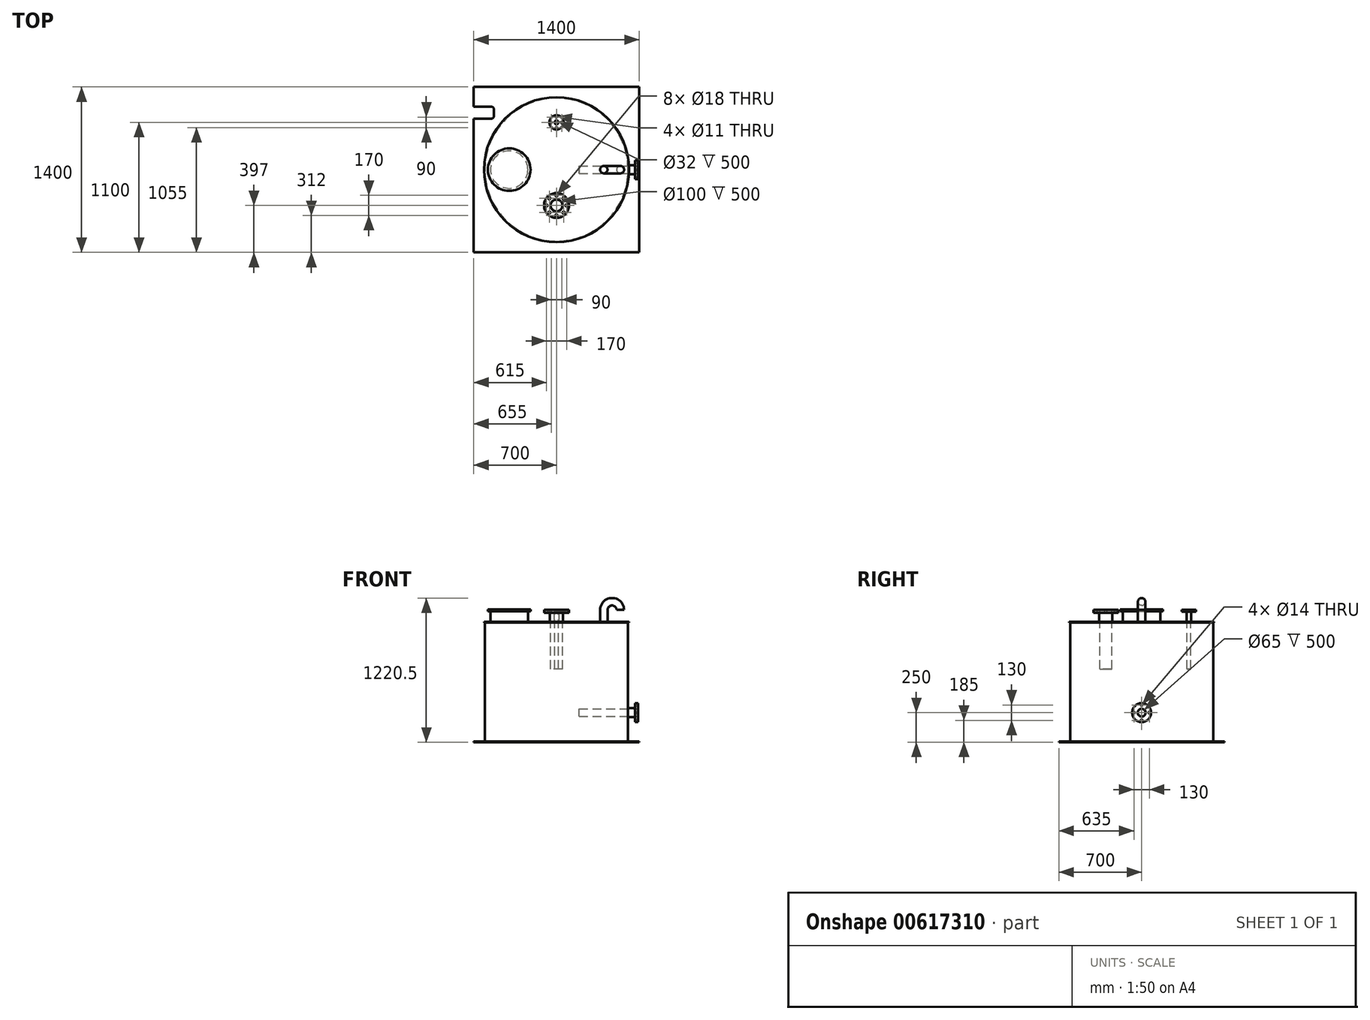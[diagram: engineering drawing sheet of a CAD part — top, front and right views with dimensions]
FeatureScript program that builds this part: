
annotation { "Feature Type Name" : "Feature", "Feature Type Description" : "" }
export const myFeature = defineFeature(function(context is Context, id is Id, definition is map)
    precondition{}
    {
        {
            var Q0;
            Q0=qCreatedBy(makeId("Front.planeOp"),FACE);
            var sketch = newSketch(context, id + "F0", { "sketchPlane" : qUnion([Q0])});
            skLineSegment(sketch, "E0.bottom", {"start": v(0, 0) * mm, "end": v(605, 0) * mm});
            skLineSegment(sketch, "E0.top", {"start": v(0, 1014) * mm, "end": v(605, 1014) * mm});
            skLineSegment(sketch, "E0.left", {"start": v(0, 0) * mm, "end": v(0, 1014) * mm});
            skLineSegment(sketch, "E0.right", {"start": v(605, 0) * mm, "end": v(605, 1006) * mm});
            skLineSegment(sketch, "E1.bottom", {"start": v(605, 1014) * mm, "end": v(613, 1014) * mm});
            skLineSegment(sketch, "E1.top", {"start": v(605, 1006) * mm, "end": v(613, 1006) * mm});
            skLineSegment(sketch, "E1.right", {"start": v(613, 1014) * mm, "end": v(613, 1006) * mm});
            skSolve(sketch);
        }
        {
            var Q0;
            Q0=makeQuery(id+"F0.imprint","IMPRINT",FACE,{"disambiguationData":[TD([[makeQuery(id+"F0.imprint","IMPRINT",EDGE,{"derivedFrom":sQuery(id+"F0.wireOp",EDGE,"E0.bottom")}),1.0]])]});
            var Q1;
            Q1=sQuery(id+"F0.wireOp",EDGE,"E0.left");
            revolve(context, id + "F1", {"entities" : qUnion([Q0]), "axis" : qUnion([Q1]), "revolveType" : RevolveType.FULL});
        }
        {
            var Q0;
            Q0=makeQuery(id+"F1.opRevolve","SWEPT_FACE",FACE,{"disambiguationData":[OSD([sQuery(id+"F0.wireOp",EDGE,"E0.bottom")])]});
            var sketch = newSketch(context, id + "F2", { "sketchPlane" : qUnion([Q0])});
            skLineSegment(sketch, "E2.bottom", {"start": v(700, 700) * mm, "end": v(-700, 700) * mm});
            skLineSegment(sketch, "E2.top", {"start": v(700, -700) * mm, "end": v(-700, -700) * mm});
            skLineSegment(sketch, "E2.left", {"start": v(700, 700) * mm, "end": v(700, -700) * mm});
            skLineSegment(sketch, "E2.right", {"start": v(-700, 700) * mm, "end": v(-700, -700) * mm});
            skPoint(sketch, "E2.middle", {"position": v(0, 0) * mm});
            skSolve(sketch);
        }
        {
            var Q0;
            Q0=makeQuery(id+"F2.imprint","IMPRINT",FACE,{"disambiguationData":[TD([[makeQuery(id+"F2.imprint","IMPRINT",EDGE,{"derivedFrom":sQuery(id+"F2.wireOp",EDGE,"E2.bottom")}),1.0]])]});
            var Q1;
            Q1=makeQuery(id+"F2.imprint","IMPRINT",FACE,{"disambiguationData":[TD([[makeQuery(id+"F2.imprint","IMPRINT",EDGE,{"derivedFrom":makeQuery(id+"F1.opRevolve","SWEPT_EDGE",EDGE,{"disambiguationData":[OSD([sQuery(id+"F0.wireOp",EDGE,"E0.bottom"),sQuery(id+"F0.wireOp",EDGE,"E0.right")])]})}),1.0]])]});
            extrude(context, id + "F3", {"entities" : qUnion([Q0, Q1]), "operationType" : NewBodyOperationType.ADD, "depth" : 5 * mm, "offsetDistance" : 25 * mm});
        }
        {
            var Q0;
            Q0=makeQuery(id+"F3.opExtrude","CAP_FACE",FACE,{"disambiguationData":[OSD([sQuery(id+"F2.wireOp",EDGE,"E2.bottom"),sQuery(id+"F2.wireOp",EDGE,"E2.top"),sQuery(id+"F2.wireOp",EDGE,"E2.left"),sQuery(id+"F2.wireOp",EDGE,"E2.right")])],"isStart":true});
            var sketch = newSketch(context, id + "F4", { "sketchPlane" : qUnion([Q0])});
            skLineSegment(sketch, "E3.bottom", {"start": v(-700, 532) * mm, "end": v(-550, 532) * mm});
            skLineSegment(sketch, "E3.top", {"start": v(-700, 432) * mm, "end": v(-550, 432) * mm});
            skLineSegment(sketch, "E3.right", {"start": v(-530, 512) * mm, "end": v(-530, 452) * mm});
            skPoint(sketch, "E4.visualSharp", {"position": v(-530, 432) * mm});
            skArc(sketch, "E4.filletArc", {"start": v(-550, 432) * mm, "mid": v(-535.86, 437.86) * mm, "end": v(-530, 452) * mm});
            skPoint(sketch, "E5.visualSharp", {"position": v(-530, 532) * mm});
            skArc(sketch, "E5.filletArc", {"start": v(-530, 512) * mm, "mid": v(-535.86, 526.14) * mm, "end": v(-550, 532) * mm});
            skLineSegment(sketch, "E6", {"start": v(-700, 432) * mm, "end": v(-700, 532) * mm});
            skSolve(sketch);
        }
        {
            var Q0;
            Q0=makeQuery(id+"F4.imprint","IMPRINT",FACE,{"disambiguationData":[TD([[makeQuery(id+"F4.imprint","IMPRINT",EDGE,{"derivedFrom":sQuery(id+"F4.wireOp",EDGE,"E3.bottom")}),-1.0]])]});
            extrude(context, id + "F5", {"entities" : qUnion([Q0]), "operationType" : NewBodyOperationType.REMOVE, "oppositeDirection" : true, "depth" : 25 * mm, "offsetDistance" : 25 * mm});
        }
        {
            var Q0;
            Q0=makeQuery(id+"F1.opRevolve","SWEPT_FACE",FACE,{"disambiguationData":[OSD([sQuery(id+"F0.wireOp",EDGE,"E0.top"),sQuery(id+"F0.wireOp",EDGE,"E1.bottom")])]});
            var sketch = newSketch(context, id + "F6", { "sketchPlane" : qUnion([Q0])});
            skCircle(sketch, "E7", {"center": v(-400, 0) * mm, "radius": 158 * mm});
            skSolve(sketch);
        }
        {
            var Q0;
            Q0=makeQuery(id+"F6.imprint","IMPRINT",FACE,{"disambiguationData":[TD([[makeQuery(id+"F6.imprint","IMPRINT",EDGE,{"derivedFrom":sQuery(id+"F6.wireOp",EDGE,"E7")}),1.0]])]});
            extrude(context, id + "F7", {"entities" : qUnion([Q0]), "operationType" : NewBodyOperationType.ADD, "depth" : 90 * mm, "offsetDistance" : 25 * mm});
        }
        {
            var Q0;
            Q0=makeQuery(id+"F7.opExtrude","CAP_FACE",FACE,{"disambiguationData":[OSD([sQuery(id+"F6.wireOp",EDGE,"E7")])],"isStart":false});
            var sketch = newSketch(context, id + "F8", { "sketchPlane" : qUnion([Q0])});
            skCircle(sketch, "E8", {"center": v(-400, 0) * mm, "radius": 180 * mm});
            skSolve(sketch);
        }
        {
            var Q0;
            Q0 = qSketchRegion(id + "F8", true);
            extrude(context, id + "F9", {"entities" : qUnion([Q0]), "operationType" : NewBodyOperationType.ADD, "depth" : 15 * mm, "offsetDistance" : 25 * mm});
        }
        {
            var Q0;
            Q0=makeQuery(id+"F1.opRevolve","SWEPT_FACE",FACE,{"disambiguationData":[OSD([sQuery(id+"F0.wireOp",EDGE,"E0.top"),sQuery(id+"F0.wireOp",EDGE,"E1.bottom")])]});
            var sketch = newSketch(context, id + "F10", { "sketchPlane" : qUnion([Q0])});
            skCircle(sketch, "E9", {"center": v(0, 400) * mm, "radius": 20 * mm});
            skCircle(sketch, "E10", {"center": v(0, -303) * mm, "radius": 55 * mm});
            skSolve(sketch);
        }
        {
            var Q0;
            Q0 = qSketchRegion(id + "F10", true);
            extrude(context, id + "F11", {"entities" : qUnion([Q0]), "operationType" : NewBodyOperationType.ADD, "depth" : 100 * mm, "offsetDistance" : 25 * mm});
        }
        {
            var Q0;
            Q0=makeQuery(id+"F11.opExtrude","CAP_FACE",FACE,{"disambiguationData":[OSD([sQuery(id+"F10.wireOp",EDGE,"E9")])],"isStart":false});
            var sketch = newSketch(context, id + "F12", { "sketchPlane" : qUnion([Q0])});
            skCircle(sketch, "E11", {"center": v(0, 400) * mm, "radius": 60 * mm});
            skCircle(sketch, "E12", {"center": v(0, 445) * mm, "radius": 5.5 * mm});
            skCircle(sketch, "E13.1.0", {"center": v(-45, 400) * mm, "radius": 5.5 * mm});
            skCircle(sketch, "E13.2.0", {"center": v(0, 355) * mm, "radius": 5.5 * mm});
            skCircle(sketch, "E13.3.0", {"center": v(45, 400) * mm, "radius": 5.5 * mm});
            skSolve(sketch);
        }
        {
            var Q0;
            Q0 = qSketchRegion(id + "F12", true);
            extrude(context, id + "F13", {"entities" : qUnion([Q0]), "operationType" : NewBodyOperationType.ADD, "oppositeDirection" : true, "depth" : 15 * mm, "offsetDistance" : 25 * mm});
        }
        {
            var Q0;
            Q0=makeQuery(id+"F13.boolean.opBoolean","MERGE",FACE,{"derivedFrom":[makeQuery(id+"F11.opExtrude","CAP_FACE",FACE,{"disambiguationData":[OSD([sQuery(id+"F10.wireOp",EDGE,"E9")])],"isStart":false}),makeQuery(id+"F13.opExtrude","CAP_FACE",FACE,{"disambiguationData":[OSD([sQuery(id+"F12.wireOp",EDGE,"E11"),sQuery(id+"F12.wireOp",EDGE,"E12"),sQuery(id+"F12.wireOp",EDGE,"E13.1.0"),sQuery(id+"F12.wireOp",EDGE,"E13.2.0"),sQuery(id+"F12.wireOp",EDGE,"E13.3.0")])],"isStart":true})]});
            var sketch = newSketch(context, id + "F14", { "sketchPlane" : qUnion([Q0])});
            skCircle(sketch, "E14", {"center": v(0, 400) * mm, "radius": 16 * mm});
            skSolve(sketch);
        }
        {
            var Q0;
            Q0 = qSketchRegion(id + "F14", true);
            extrude(context, id + "F15", {"entities" : qUnion([Q0]), "operationType" : NewBodyOperationType.REMOVE, "oppositeDirection" : true, "depth" : 500 * mm, "offsetDistance" : 25 * mm});
        }
        {
            var Q0;
            Q0=makeQuery(id+"F11.opExtrude","CAP_FACE",FACE,{"disambiguationData":[OSD([sQuery(id+"F10.wireOp",EDGE,"E10")])],"isStart":false});
            var sketch = newSketch(context, id + "F16", { "sketchPlane" : qUnion([Q0])});
            skCircle(sketch, "E15", {"center": v(0, -303) * mm, "radius": 105 * mm});
            skCircle(sketch, "E16", {"center": v(0, -218) * mm, "radius": 9 * mm});
            skCircle(sketch, "E17.1.0", {"center": v(-60.1, -242.9) * mm, "radius": 9 * mm});
            skCircle(sketch, "E17.2.0", {"center": v(-85, -303) * mm, "radius": 9 * mm});
            skCircle(sketch, "E17.3.0", {"center": v(-60.1, -363.1) * mm, "radius": 9 * mm});
            skCircle(sketch, "E17.4.0", {"center": v(0, -388) * mm, "radius": 9 * mm});
            skCircle(sketch, "E17.5.0", {"center": v(60.1, -363.1) * mm, "radius": 9 * mm});
            skCircle(sketch, "E17.6.0", {"center": v(85, -303) * mm, "radius": 9 * mm});
            skCircle(sketch, "E17.7.0", {"center": v(60.1, -242.9) * mm, "radius": 9 * mm});
            skSolve(sketch);
        }
        {
            var Q0;
            Q0 = qSketchRegion(id + "F16", true);
            extrude(context, id + "F17", {"entities" : qUnion([Q0]), "operationType" : NewBodyOperationType.ADD, "oppositeDirection" : true, "depth" : 25 * mm, "offsetDistance" : 25 * mm});
        }
        {
            var Q0;
            Q0=makeQuery(id+"F17.boolean.opBoolean","MERGE",FACE,{"derivedFrom":[makeQuery(id+"F11.opExtrude","CAP_FACE",FACE,{"disambiguationData":[OSD([sQuery(id+"F10.wireOp",EDGE,"E10")])],"isStart":false}),makeQuery(id+"F17.opExtrude","CAP_FACE",FACE,{"disambiguationData":[OSD([sQuery(id+"F16.wireOp",EDGE,"E15"),sQuery(id+"F16.wireOp",EDGE,"E16"),sQuery(id+"F16.wireOp",EDGE,"E17.1.0"),sQuery(id+"F16.wireOp",EDGE,"E17.2.0"),sQuery(id+"F16.wireOp",EDGE,"E17.3.0"),sQuery(id+"F16.wireOp",EDGE,"E17.4.0"),sQuery(id+"F16.wireOp",EDGE,"E17.5.0"),sQuery(id+"F16.wireOp",EDGE,"E17.6.0"),sQuery(id+"F16.wireOp",EDGE,"E17.7.0")])],"isStart":true})]});
            var sketch = newSketch(context, id + "F18", { "sketchPlane" : qUnion([Q0])});
            skCircle(sketch, "E18", {"center": v(0, -303) * mm, "radius": 50 * mm});
            skSolve(sketch);
        }
        {
            var Q0;
            Q0=makeQuery(id+"F18.imprint","IMPRINT",FACE,{"disambiguationData":[TD([[makeQuery(id+"F18.imprint","IMPRINT",EDGE,{"derivedFrom":sQuery(id+"F18.wireOp",EDGE,"E18")}),1.0]])]});
            extrude(context, id + "F19", {"entities" : qUnion([Q0]), "operationType" : NewBodyOperationType.REMOVE, "oppositeDirection" : true, "depth" : 500 * mm, "offsetDistance" : 25 * mm});
        }
        {
            var Q0;
            Q0=makeQuery(id+"F1.opRevolve","SWEPT_FACE",FACE,{"disambiguationData":[OSD([sQuery(id+"F0.wireOp",EDGE,"E0.top"),sQuery(id+"F0.wireOp",EDGE,"E1.bottom")])]});
            var sketch = newSketch(context, id + "F20", { "sketchPlane" : qUnion([Q0])});
            skCircle(sketch, "E19", {"center": v(400, 0) * mm, "radius": 31.5 * mm});
            skSolve(sketch);
        }
        {
            var Q0;
            Q0=qCreatedBy(makeId("Front.planeOp"),FACE);
            var sketch = newSketch(context, id + "F21", { "sketchPlane" : qUnion([Q0])});
            skPoint(sketch, "E20.0", {"position": v(400, 1014) * mm});
            skLineSegment(sketch, "E21", {"start": v(400, 1014) * mm, "end": v(400, 1114) * mm});
            skArc(sketch, "E22", {"start": v(540, 1114) * mm, "mid": v(470, 1184) * mm, "end": v(400, 1114) * mm});
            skSolve(sketch);
        }
        {
            var Q0;
            Q0=makeQuery(id+"F20.imprint","IMPRINT",FACE,{"disambiguationData":[TD([[makeQuery(id+"F20.imprint","IMPRINT",EDGE,{"derivedFrom":sQuery(id+"F20.wireOp",EDGE,"E19")}),1.0]])]});
            var Q1;
            Q1=sQuery(id+"F21.wireOp",EDGE,"E21");
            var Q2;
            Q2=sQuery(id+"F21.wireOp",EDGE,"E22");
            sweep(context, id + "F22", {"operationType" : NewBodyOperationType.ADD, "profiles" : qUnion([Q0]), "path" : qUnion([Q1, Q2])});
        }
        {
            var Q0;
            Q0=qCreatedBy(makeId("Right.planeOp"),FACE);
            var sketch = newSketch(context, id + "F23", { "sketchPlane" : qUnion([Q0])});
            skCircle(sketch, "E23", {"center": v(0, 245) * mm, "radius": 37.5 * mm});
            skSolve(sketch);
        }
        {
            var Q0;
            Q0 = qSketchRegion(id + "F23", true);
            extrude(context, id + "F24", {"entities" : qUnion([Q0]), "operationType" : NewBodyOperationType.ADD, "depth" : 690 * mm, "offsetDistance" : 25 * mm});
        }
        {
            var Q0;
            Q0=makeQuery(id+"F24.opExtrude","CAP_FACE",FACE,{"disambiguationData":[OSD([sQuery(id+"F23.wireOp",EDGE,"E23")])],"isStart":false});
            var sketch = newSketch(context, id + "F25", { "sketchPlane" : qUnion([Q0])});
            skCircle(sketch, "E24", {"center": v(0, 245) * mm, "radius": 80 * mm});
            skCircle(sketch, "E25", {"center": v(0, 310) * mm, "radius": 7 * mm});
            skCircle(sketch, "E26.1.0", {"center": v(-65, 245) * mm, "radius": 7 * mm});
            skCircle(sketch, "E26.2.0", {"center": v(0, 180) * mm, "radius": 7 * mm});
            skCircle(sketch, "E26.3.0", {"center": v(65, 245) * mm, "radius": 7 * mm});
            skSolve(sketch);
        }
        {
            var Q0;
            Q0 = qSketchRegion(id + "F25", true);
            extrude(context, id + "F26", {"entities" : qUnion([Q0]), "operationType" : NewBodyOperationType.ADD, "oppositeDirection" : true, "depth" : 25 * mm, "offsetDistance" : 25 * mm});
        }
        {
            var Q0;
            Q0=makeQuery(id+"F26.boolean.opBoolean","MERGE",FACE,{"derivedFrom":[makeQuery(id+"F24.opExtrude","CAP_FACE",FACE,{"disambiguationData":[OSD([sQuery(id+"F23.wireOp",EDGE,"E23")])],"isStart":false}),makeQuery(id+"F26.opExtrude","CAP_FACE",FACE,{"disambiguationData":[OSD([sQuery(id+"F25.wireOp",EDGE,"E24"),sQuery(id+"F25.wireOp",EDGE,"E25"),sQuery(id+"F25.wireOp",EDGE,"E26.1.0"),sQuery(id+"F25.wireOp",EDGE,"E26.2.0"),sQuery(id+"F25.wireOp",EDGE,"E26.3.0")])],"isStart":true})]});
            var sketch = newSketch(context, id + "F27", { "sketchPlane" : qUnion([Q0])});
            skCircle(sketch, "E27", {"center": v(0, 245) * mm, "radius": 32.5 * mm});
            skSolve(sketch);
        }
        {
            var Q0;
            Q0=makeQuery(id+"F27.imprint","IMPRINT",FACE,{"disambiguationData":[TD([[makeQuery(id+"F27.imprint","IMPRINT",EDGE,{"derivedFrom":sQuery(id+"F27.wireOp",EDGE,"E27")}),1.0]])]});
            extrude(context, id + "F28", {"entities" : qUnion([Q0]), "operationType" : NewBodyOperationType.REMOVE, "oppositeDirection" : true, "depth" : 500 * mm, "offsetDistance" : 25 * mm});
        }
    });
